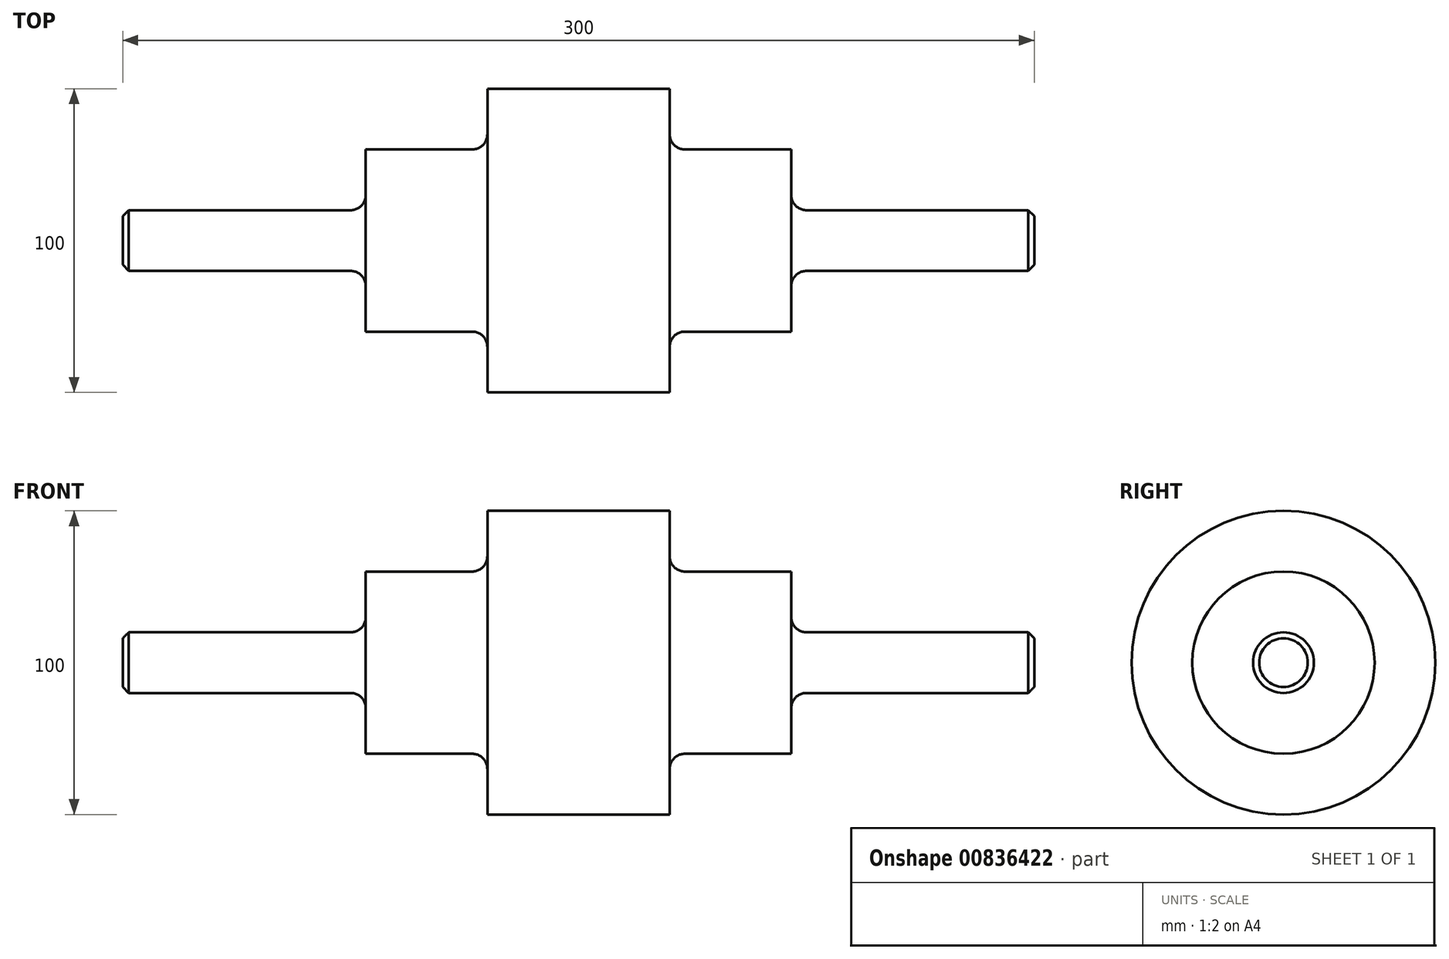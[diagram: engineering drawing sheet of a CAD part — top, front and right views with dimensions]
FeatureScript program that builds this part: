
annotation { "Feature Type Name" : "Feature", "Feature Type Description" : "" }
export const myFeature = defineFeature(function(context is Context, id is Id, definition is map)
    precondition{}
    {
        {
            var Q0;
            Q0=qCreatedBy(makeId("Top.planeOp"),FACE);
            var sketch = newSketch(context, id + "F0", { "sketchPlane" : qUnion([Q0])});
            skLineSegment(sketch, "E0", {"start": v(-150, 0) * mm, "end": v(150, 0) * mm});
            skLineSegment(sketch, "E1", {"start": v(-150, 0) * mm, "end": v(-150, 10) * mm});
            skLineSegment(sketch, "E2", {"start": v(-150, 10) * mm, "end": v(-70, 10) * mm});
            skLineSegment(sketch, "E3", {"start": v(-70, 10) * mm, "end": v(-70, 30) * mm});
            skLineSegment(sketch, "E4", {"start": v(-70, 30) * mm, "end": v(-30, 30) * mm});
            skLineSegment(sketch, "E5", {"start": v(-30, 30) * mm, "end": v(-30, 50) * mm});
            skLineSegment(sketch, "E6", {"start": v(-30, 50) * mm, "end": v(30, 50) * mm});
            skLineSegment(sketch, "E7", {"start": v(30, 50) * mm, "end": v(30, 30) * mm});
            skLineSegment(sketch, "E8", {"start": v(30, 30) * mm, "end": v(70, 30) * mm});
            skLineSegment(sketch, "E9", {"start": v(70, 30) * mm, "end": v(70, 10) * mm});
            skLineSegment(sketch, "E10", {"start": v(70, 10) * mm, "end": v(150, 10) * mm});
            skLineSegment(sketch, "E11", {"start": v(150, 10) * mm, "end": v(150, 0) * mm});
            skSolve(sketch);
        }
        {
            var Q0;
            Q0 = qSketchRegion(id + "F0", true);
            var Q1;
            Q1=sQuery(id+"F0.wireOp",EDGE,"E0");
            revolve(context, id + "F1", {"surfaceOperationType" : NewSurfaceOperationType.NEW, "entities" : qUnion([Q0]), "axis" : qUnion([Q1]), "revolveType" : RevolveType.FULL});
        }
        {
            var Q0;
            Q0=makeQuery(id+"F1.opRevolve","SWEPT_EDGE",EDGE,{"disambiguationData":[OSD([sQuery(id+"F0.wireOp",EDGE,"E4"),sQuery(id+"F0.wireOp",EDGE,"E5")])]});
            var Q1;
            Q1=makeQuery(id+"F1.opRevolve","SWEPT_EDGE",EDGE,{"disambiguationData":[OSD([sQuery(id+"F0.wireOp",EDGE,"E7"),sQuery(id+"F0.wireOp",EDGE,"E8")])]});
            fillet(context, id + "F2", {"entities" : qUnion([Q0, Q1]), "radius" : 5 * mm, "tangentPropagation" : true, "allowEdgeOverflow" : false});
        }
        {
            var Q0;
            Q0=makeQuery(id+"F1.opRevolve","SWEPT_EDGE",EDGE,{"disambiguationData":[OSD([sQuery(id+"F0.wireOp",EDGE,"E1"),sQuery(id+"F0.wireOp",EDGE,"E2")])]});
            var Q1;
            Q1=makeQuery(id+"F1.opRevolve","SWEPT_EDGE",EDGE,{"disambiguationData":[OSD([sQuery(id+"F0.wireOp",EDGE,"E10"),sQuery(id+"F0.wireOp",EDGE,"E11")])]});
            chamfer(context, id + "F3", {"entities" : qUnion([Q0, Q1]), "width" : 2 * mm, "tangentPropagation" : true});
        }
        {
            var Q0;
            Q0=makeQuery(id+"F1.opRevolve","SWEPT_EDGE",EDGE,{"disambiguationData":[OSD([sQuery(id+"F0.wireOp",EDGE,"E2"),sQuery(id+"F0.wireOp",EDGE,"E3")])]});
            var Q1;
            Q1=makeQuery(id+"F1.opRevolve","SWEPT_EDGE",EDGE,{"disambiguationData":[OSD([sQuery(id+"F0.wireOp",EDGE,"E9"),sQuery(id+"F0.wireOp",EDGE,"E10")])]});
            fillet(context, id + "F4", {"entities" : qUnion([Q0, Q1]), "radius" : 5 * mm, "tangentPropagation" : true, "allowEdgeOverflow" : false});
        }
    });
